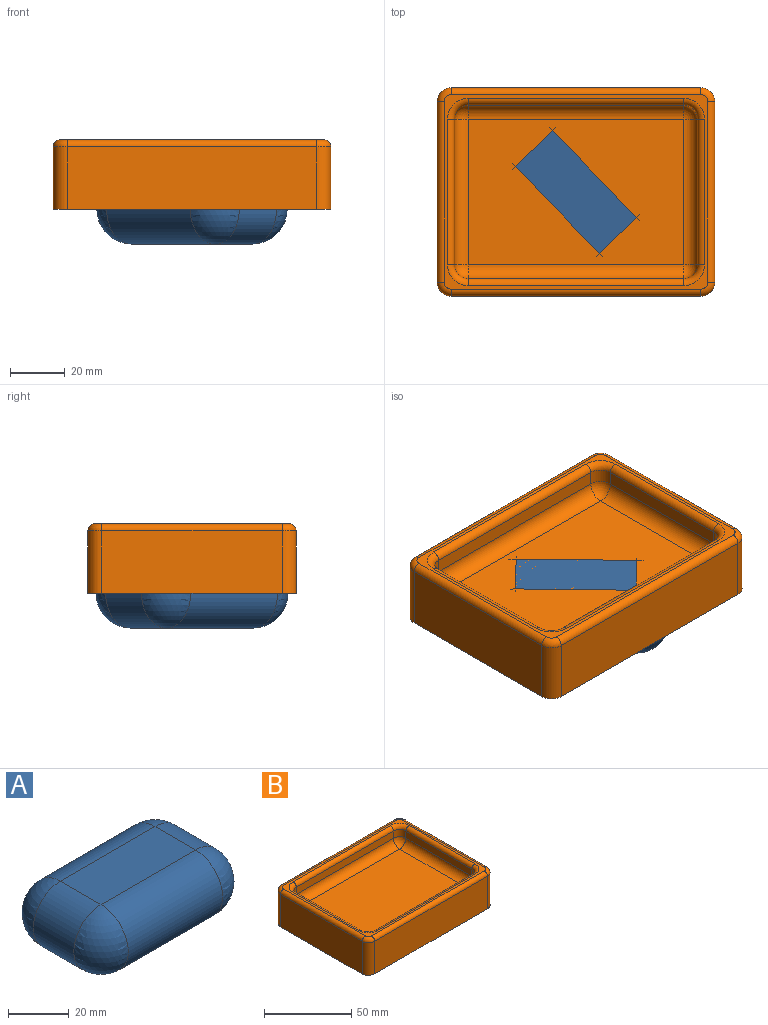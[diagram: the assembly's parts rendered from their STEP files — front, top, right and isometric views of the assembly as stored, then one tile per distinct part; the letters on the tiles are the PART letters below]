
ASSEMBLY  parts=2 mates=1
PART A: 10 faces, bbox 69.5x44.3x25.4 mm
  f0: plane 44.13x18.92mm, normal (0,0,1), area 835.1mm2, adj f3,f4,f7,f8
  f1: plane 44.13x18.92mm, normal (0,0,-1), area 835.1mm2, adj f3,f4,f7,f8
  f2: sphere r=12.7mm, area 506.7mm2, adj f3,f4
  f3: cylinder r=12.7mm len=44.13mm, axis (1,0,0), area 1760.7mm2, adj f0,f1,f2,f5
  f4: cylinder r=12.7mm len=25.4mm, axis (0,-1,0), area 755mm2, adj f0,f1,f2,f6
  f5: sphere r=12.7mm, area 506.7mm2, adj f3,f7
  f6: sphere r=12.7mm, area 506.7mm2, adj f4,f8
  f7: cylinder r=12.7mm len=25.4mm, axis (0,1,0), area 755mm2, adj f0,f1,f5,f9
  f8: cylinder r=12.7mm len=44.13mm, axis (-1,0,0), area 1760.7mm2, adj f0,f1,f6,f9
  f9: sphere r=12.7mm, area 506.7mm2, adj f7,f8
PART B: 61 faces, bbox 102.4x77x25.4 mm
  f0: plane 101.6x76.2mm, normal (0,0,-1), area 860.8mm2, adj f1,f2,f3,f4,f15,f16,f17,f18
  f1: plane 66.04x22.86mm, normal (-1,0,0), area 1509.7mm2, adj f0,f15,f18,f32
  f2: plane 91.44x22.86mm, normal (0,-1,0), area 2090.3mm2, adj f0,f15,f16,f33
  f3: plane 66.04x22.86mm, normal (1,0,0), area 1509.7mm2, adj f0,f16,f17,f29
  f4: plane 91.44x22.86mm, normal (0,1,0), area 2090.3mm2, adj f0,f17,f18,f28
  f5: plane 96.52x71.12mm, normal (0,0,1), area 463.7mm2, adj f19,f20,f21,f22,f23,f24,f25,f26
  f6: plane 53.34x5.08mm, normal (1,0,0), area 271mm2, adj f11,f14,f24,f54
  f7: plane 78.74x5.08mm, normal (0,1,0), area 400mm2, adj f11,f12,f20,f58
  f8: plane 53.34x5.08mm, normal (-1,0,0), area 271mm2, adj f12,f13,f21,f59
  f9: plane 78.74x5.08mm, normal (0,-1,0), area 400mm2, adj f13,f14,f25,f55
  f10: plane 78.74x53.34mm, normal (0,0,1), area 4200mm2, adj f54,f55,f58,f59
  f11: cylinder r=5.08mm len=5.08mm, axis (0,0,-1), area 40.5mm2, adj f6,f7,f22,f56
  f12: cylinder r=5.08mm len=5.08mm, axis (0,0,1), area 40.5mm2, adj f7,f8,f19,f60
  f13: cylinder r=5.08mm len=5.08mm, axis (0,0,-1), area 40.5mm2, adj f8,f9,f23,f57
  f14: cylinder r=5.08mm len=5.08mm, axis (0,0,1), area 40.5mm2, adj f6,f9,f26,f53
  f15: cylinder r=5.08mm len=22.86mm, axis (0,0,-1), area 182.4mm2, adj f0,f1,f2,f34
  f16: cylinder r=5.08mm len=22.86mm, axis (0,0,1), area 182.4mm2, adj f0,f2,f3,f31
  f17: cylinder r=5.08mm len=22.86mm, axis (0,0,-1), area 182.4mm2, adj f0,f3,f4,f27
  f18: cylinder r=5.08mm len=22.86mm, axis (0,0,1), area 182.4mm2, adj f0,f1,f4,f30
  f19: torus R=7.62mm, axis (0,0,1), area 37.6mm2, adj f5,f12,f20,f21
  f20: cylinder r=2.54mm len=78.74mm, axis (-1,0,0), area 314.2mm2, adj f5,f7,f19,f22
  f21: cylinder r=2.54mm len=53.34mm, axis (0,-1,0), area 212.8mm2, adj f5,f8,f19,f23
  f22: torus R=7.62mm, axis (0,0,1), area 37.6mm2, adj f5,f11,f20,f24
  f23: torus R=7.62mm, axis (0,0,1), area 37.6mm2, adj f5,f13,f21,f25
  f24: cylinder r=2.54mm len=53.34mm, axis (0,1,0), area 212.8mm2, adj f5,f6,f22,f26
  f25: cylinder r=2.54mm len=78.74mm, axis (1,0,0), area 314.2mm2, adj f5,f9,f23,f26
  f26: torus R=7.62mm, axis (0,0,1), area 37.6mm2, adj f5,f14,f24,f25
  f27: torus R=2.54mm, axis (0,0,1), area 26.1mm2, adj f5,f17,f28,f29
  f28: cylinder r=2.54mm len=91.44mm, axis (1,0,0), area 364.8mm2, adj f4,f5,f27,f30
  f29: cylinder r=2.54mm len=66.04mm, axis (0,-1,0), area 263.5mm2, adj f3,f5,f27,f31
  f30: torus R=2.54mm, axis (0,0,1), area 26.1mm2, adj f5,f18,f28,f32
  f31: torus R=2.54mm, axis (0,0,1), area 26.1mm2, adj f5,f16,f29,f33
  f32: cylinder r=2.54mm len=66.04mm, axis (0,1,0), area 263.5mm2, adj f1,f5,f30,f34
  f33: cylinder r=2.54mm len=91.44mm, axis (-1,0,0), area 364.8mm2, adj f2,f5,f31,f34
  f34: torus R=2.54mm, axis (0,0,1), area 26.1mm2, adj f5,f15,f32,f33
  f35: plane 66.04x22.86mm, normal (1,0,0), area 1509.7mm2, adj f0,f39,f49,f52
  f36: plane 91.44x22.86mm, normal (0,1,0), area 2090.3mm2, adj f0,f39,f49,f50
  f37: plane 66.04x22.86mm, normal (-1,0,0), area 1509.7mm2, adj f0,f39,f50,f51
  f38: plane 91.44x22.86mm, normal (0,-1,0), area 2090.3mm2, adj f0,f39,f51,f52
  f39: plane 96.52x71.12mm, normal (0,0,-1), area 463.7mm2, adj f35,f36,f37,f38,f40,f41,f42,f43
  f40: plane 53.34x12.7mm, normal (-1,0,0), area 677.4mm2, adj f39,f44,f45,f48
  f41: plane 78.74x12.7mm, normal (0,-1,0), area 1000mm2, adj f39,f44,f45,f46
  f42: plane 53.34x12.7mm, normal (1,0,0), area 677.4mm2, adj f39,f44,f46,f47
  f43: plane 78.74x12.7mm, normal (0,1,0), area 1000mm2, adj f39,f44,f47,f48
  f44: plane 93.98x68.58mm, normal (0,0,-1), area 6395.3mm2, adj f40,f41,f42,f43,f45,f46,f47,f48
  f45: cylinder r=7.62mm len=12.7mm, axis (0,0,-1), area 152mm2, adj f39,f40,f41,f44
  f46: cylinder r=7.62mm len=12.7mm, axis (0,0,1), area 152mm2, adj f39,f41,f42,f44
  f47: cylinder r=7.62mm len=12.7mm, axis (0,0,-1), area 152mm2, adj f39,f42,f43,f44
  f48: cylinder r=7.62mm len=12.7mm, axis (0,0,1), area 152mm2, adj f39,f40,f43,f44
  f49: cylinder r=2.54mm len=22.86mm, axis (0,0,-1), area 91.2mm2, adj f0,f35,f36,f39
  f50: cylinder r=2.54mm len=22.86mm, axis (0,0,1), area 91.2mm2, adj f0,f36,f37,f39
  f51: cylinder r=2.54mm len=22.86mm, axis (0,0,-1), area 91.2mm2, adj f0,f37,f38,f39
  f52: cylinder r=2.54mm len=22.86mm, axis (0,0,1), area 91.2mm2, adj f0,f35,f38,f39
  f53: sphere r=5.08mm, area 40.5mm2, adj f14,f54,f55
  f54: cylinder r=5.08mm len=53.34mm, axis (0,-1,0), area 425.6mm2, adj f6,f10,f53,f56
  f55: cylinder r=5.08mm len=78.74mm, axis (-1,0,0), area 628.3mm2, adj f9,f10,f53,f57
  f56: sphere r=5.08mm, area 40.5mm2, adj f11,f54,f58
  f57: sphere r=5.08mm, area 40.5mm2, adj f13,f55,f59
  f58: cylinder r=5.08mm len=78.74mm, axis (1,0,0), area 628.3mm2, adj f7,f10,f56,f60
  f59: cylinder r=5.08mm len=53.34mm, axis (0,1,0), area 425.6mm2, adj f8,f10,f57,f60
  f60: sphere r=5.08mm, area 40.5mm2, adj f12,f58,f59
PLACE A rot(axis=(0,0,-1),46.1deg) t=(2.96,0.79,-25.39)mm
PLACE B rot(axis=(-0.65,-0.17,-0.74),0deg) t=(2.96,0.79,0.01)mm fixed
MATE revolute A.f0 <-> B.f10  axis (0,0,1) through (2.96,0.79,12.71)mm
